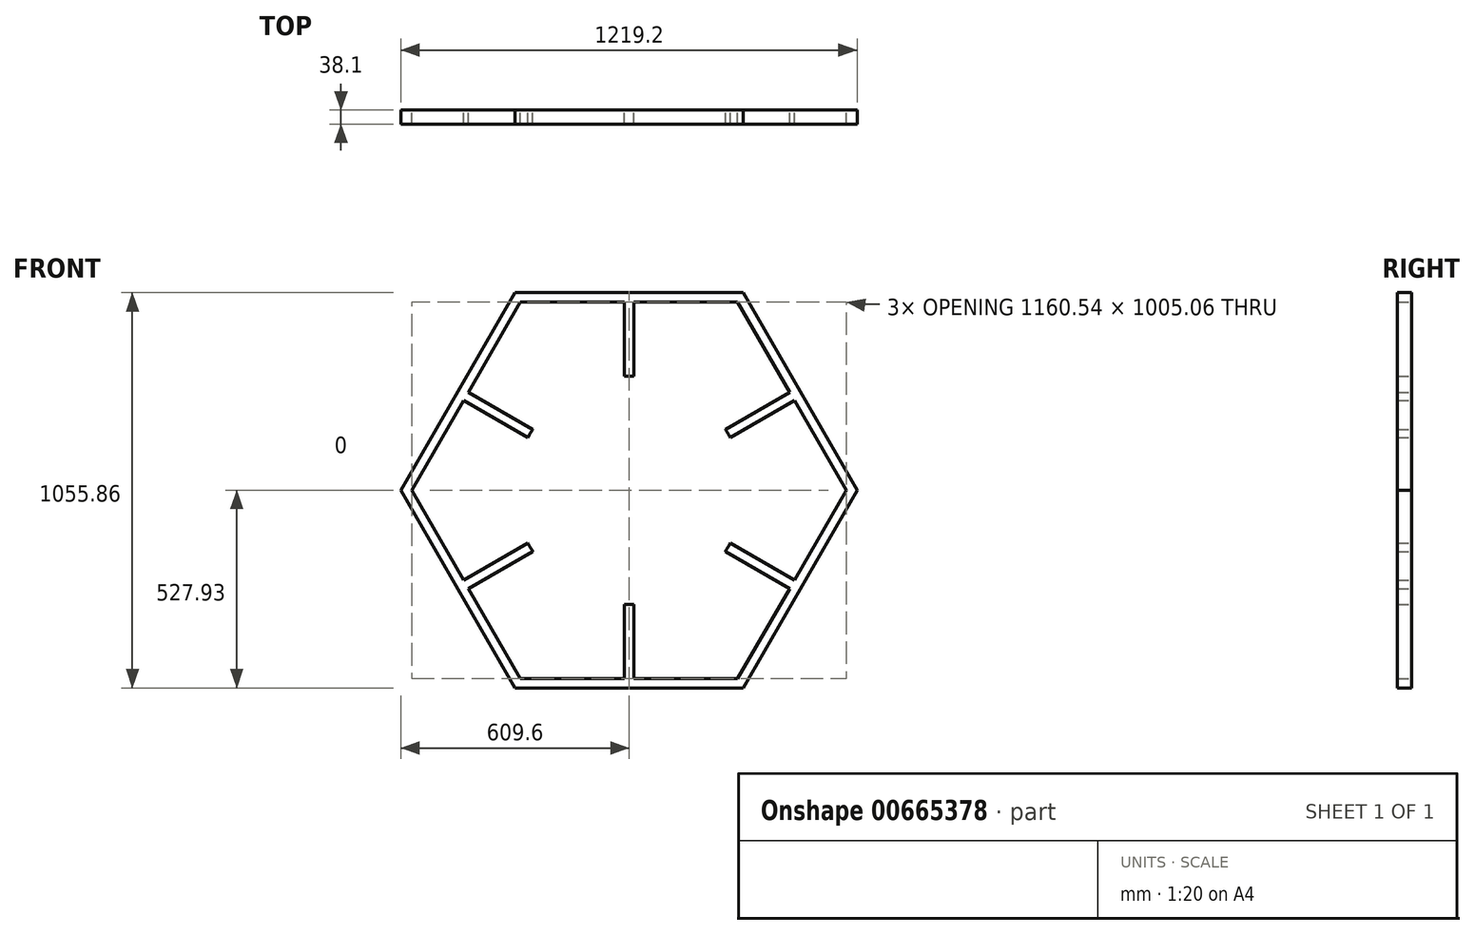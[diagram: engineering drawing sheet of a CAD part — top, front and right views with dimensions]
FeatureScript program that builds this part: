
annotation { "Feature Type Name" : "Feature", "Feature Type Description" : "" }
export const myFeature = defineFeature(function(context is Context, id is Id, definition is map)
    precondition{}
    {
        {
            var Q0;
            Q0=qCreatedBy(makeId("Front.planeOp"),FACE);
            var sketch = newSketch(context, id + "F0", { "sketchPlane" : qUnion([Q0])});
            skCircle(sketch, "E0.cCircle", {"center": v(0, 0) * mm, "radius": 502.53 * mm, "construction": true});
            skLineSegment(sketch, "E0.0", {"start": v(290.14, 502.53) * mm, "end": v(580.27, 0) * mm});
            skLineSegment(sketch, "E0.1", {"start": v(580.27, 0) * mm, "end": v(290.14, -502.53) * mm});
            skLineSegment(sketch, "E0.2", {"start": v(290.14, -502.53) * mm, "end": v(-290.14, -502.53) * mm});
            skLineSegment(sketch, "E0.3", {"start": v(-290.14, -502.53) * mm, "end": v(-580.27, 0) * mm});
            skLineSegment(sketch, "E0.4", {"start": v(-580.27, 0) * mm, "end": v(-428.85, 262.26) * mm});
            skLineSegment(sketch, "E0.5", {"start": v(-290.14, 502.53) * mm, "end": v(290.14, 502.53) * mm});
            skPoint(sketch, "E0.0.midPoint", {"position": v(435.2, 251.26) * mm});
            skCircle(sketch, "E1", {"center": v(0, 0) * mm, "radius": 304.8 * mm});
            skLineSegment(sketch, "E2", {"start": v(-441.55, 240.27) * mm, "end": v(-270.09, 141.27) * mm});
            skLineSegment(sketch, "E3", {"start": v(-428.85, 262.26) * mm, "end": v(-257.39, 163.27) * mm});
            skLineSegment(sketch, "E4", {"start": v(-290.14, 502.53) * mm, "end": v(-290.14, 502.53) * mm});
            skLineSegment(sketch, "E5", {"start": v(-441.55, 240.27) * mm, "end": v(-290.14, 502.53) * mm});
            skLineSegment(sketch, "E6", {"start": v(-460.1, 208.14) * mm, "end": v(-428.85, 262.26) * mm});
            skLineSegment(sketch, "E7", {"start": v(-580.27, 0) * mm, "end": v(-580.27, 0) * mm});
            skPoint(sketch, "E8.center", {"position": v(38, -49.16) * mm});
            skLineSegment(sketch, "E9", {"start": v(-1099.5, 304.8) * mm, "end": v(1284.02, 304.8) * mm, "construction": true});
            skLineSegment(sketch, "E10", {"start": v(-1101.82, -304.8) * mm, "end": v(1466.6, -304.8) * mm, "construction": true});
            skLineSegment(sketch, "E11.1.0", {"start": v(-428.85, -262.26) * mm, "end": v(-257.39, -163.27) * mm});
            skLineSegment(sketch, "E11.1.1", {"start": v(-441.55, -240.27) * mm, "end": v(-270.09, -141.27) * mm});
            skLineSegment(sketch, "E11.2.0", {"start": v(12.7, -502.53) * mm, "end": v(12.7, -304.54) * mm});
            skLineSegment(sketch, "E11.2.1", {"start": v(-12.7, -502.53) * mm, "end": v(-12.7, -304.54) * mm});
            skLineSegment(sketch, "E11.3.0", {"start": v(441.55, -240.27) * mm, "end": v(270.09, -141.27) * mm});
            skLineSegment(sketch, "E11.3.1", {"start": v(428.85, -262.26) * mm, "end": v(257.39, -163.27) * mm});
            skLineSegment(sketch, "E11.4.0", {"start": v(428.85, 262.26) * mm, "end": v(257.39, 163.27) * mm});
            skLineSegment(sketch, "E11.4.1", {"start": v(441.55, 240.27) * mm, "end": v(270.09, 141.27) * mm});
            skLineSegment(sketch, "E11.5.0", {"start": v(-12.7, 502.53) * mm, "end": v(-12.7, 304.54) * mm});
            skLineSegment(sketch, "E11.5.1", {"start": v(12.7, 502.53) * mm, "end": v(12.7, 304.54) * mm});
            skCircle(sketch, "E12.cCircle", {"center": v(0, 0) * mm, "radius": 527.93 * mm, "construction": true});
            skLineSegment(sketch, "E12.0", {"start": v(-304.8, 527.93) * mm, "end": v(304.8, 527.93) * mm});
            skLineSegment(sketch, "E12.1", {"start": v(304.8, 527.93) * mm, "end": v(609.6, 0) * mm});
            skLineSegment(sketch, "E12.2", {"start": v(609.6, 0) * mm, "end": v(304.8, -527.93) * mm});
            skLineSegment(sketch, "E12.3", {"start": v(304.8, -527.93) * mm, "end": v(-304.8, -527.93) * mm});
            skLineSegment(sketch, "E12.4", {"start": v(-304.8, -527.93) * mm, "end": v(-609.6, 0) * mm});
            skLineSegment(sketch, "E12.5", {"start": v(-609.6, 0) * mm, "end": v(-304.8, 527.93) * mm});
            skPoint(sketch, "E12.0.midPoint", {"position": v(0, 527.93) * mm});
            skSolve(sketch);
        }
        {
            var Q0;
            {var subQ0=sQuery(id+"F0.wireOp",EDGE,"E11.5.0");Q0=makeQuery(id+"F0.imprint","IMPRINT",FACE,{"disambiguationData":[TD([[makeQuery(id+"F0.imprint","IMPRINT",EDGE,{"derivedFrom":subQ0}),1.0]])]});}
            var Q1;
            {var subQ0=sQuery(id+"F0.wireOp",EDGE,"E2");Q1=makeQuery(id+"F0.imprint","IMPRINT",FACE,{"disambiguationData":[TD([[makeQuery(id+"F0.imprint","IMPRINT",EDGE,{"derivedFrom":subQ0}),1.0]])]});}
            var Q2;
            {var subQ0=sQuery(id+"F0.wireOp",EDGE,"E11.4.0");Q2=makeQuery(id+"F0.imprint","IMPRINT",FACE,{"disambiguationData":[TD([[makeQuery(id+"F0.imprint","IMPRINT",EDGE,{"derivedFrom":subQ0}),1.0]])]});}
            var Q3;
            {var subQ0=sQuery(id+"F0.wireOp",EDGE,"E11.3.0");Q3=makeQuery(id+"F0.imprint","IMPRINT",FACE,{"disambiguationData":[TD([[makeQuery(id+"F0.imprint","IMPRINT",EDGE,{"derivedFrom":subQ0}),1.0]])]});}
            var Q4;
            {var subQ0=sQuery(id+"F0.wireOp",EDGE,"E11.2.0");Q4=makeQuery(id+"F0.imprint","IMPRINT",FACE,{"disambiguationData":[TD([[makeQuery(id+"F0.imprint","IMPRINT",EDGE,{"derivedFrom":subQ0}),1.0]])]});}
            var Q5;
            {var subQ0=sQuery(id+"F0.wireOp",EDGE,"E11.1.0");Q5=makeQuery(id+"F0.imprint","IMPRINT",FACE,{"disambiguationData":[TD([[makeQuery(id+"F0.imprint","IMPRINT",EDGE,{"derivedFrom":subQ0}),1.0]])]});}
            var Q6;
            {var subQ6=sQuery(id+"F0.wireOp",EDGE,"E0.4");Q6=makeQuery(id+"F0.imprint","IMPRINT",FACE,{"disambiguationData":[TD([[makeQuery(id+"F0.imprint","IMPRINT",EDGE,{"derivedFrom":subQ6}),1.0]])]});}
            extrude(context, id + "F1", {"entities" : qUnion([Q0, Q1, Q2, Q3, Q4, Q5, Q6]), "depth" : 38.1 * mm, "offsetDistance" : 25.4 * mm});
        }
    });
